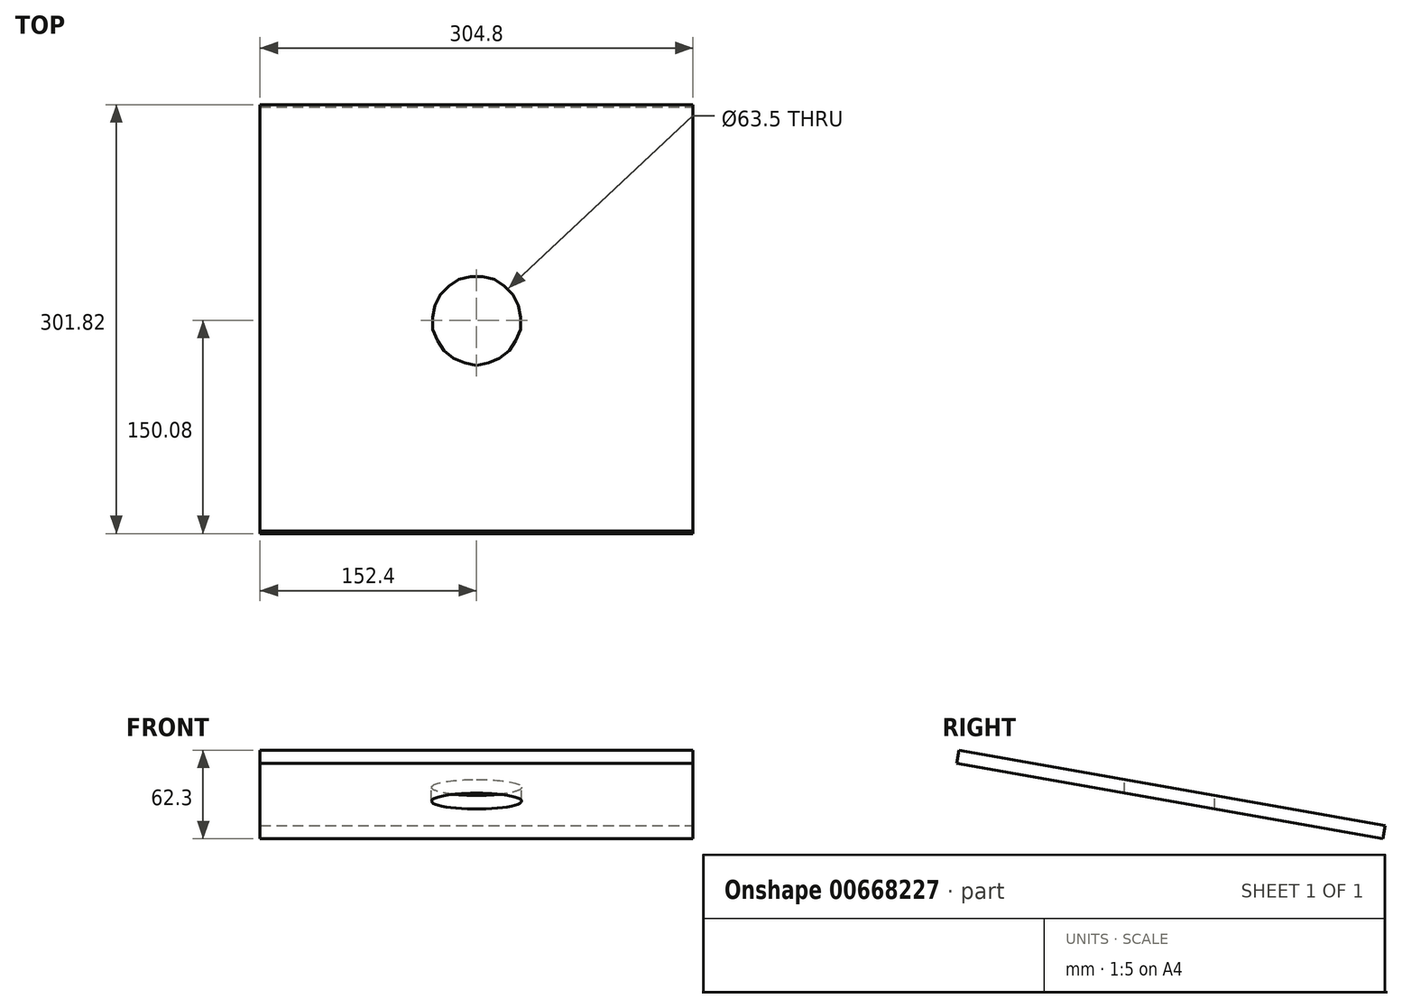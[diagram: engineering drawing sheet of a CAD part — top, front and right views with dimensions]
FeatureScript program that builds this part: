
annotation { "Feature Type Name" : "Feature", "Feature Type Description" : "" }
export const myFeature = defineFeature(function(context is Context, id is Id, definition is map)
    precondition{}
    {
        {
            var Q0;
            Q0=qCreatedBy(makeId("Top.planeOp"),FACE);
            var sketch = newSketch(context, id + "F0", { "sketchPlane" : qUnion([Q0])});
            skLineSegment(sketch, "E0", {"start": v(0, 0) * mm, "end": v(53.06, 0) * mm, "construction": true});
            skSolve(sketch);
        }
        {
            var Q0;
            Q0=sQuery(id+"F0.wireOp",EDGE,"E0");
            cPlane(context, id + "F1", {"entities" : qUnion([Q0]), "cplaneType" : CPlaneType.LINE_ANGLE, "offset" : 25 * mm, "angle" : 80 * degree, "width" : 150 * mm, "height" : 150 * mm});
        }
        {
            var Q0;
            Q0=qCreatedBy(id+"F1.planeOp",FACE);
            var sketch = newSketch(context, id + "F2", { "sketchPlane" : qUnion([Q0])});
            skLineSegment(sketch, "E1.bottom", {"start": v(-152.4, -152.4) * mm, "end": v(152.4, -152.4) * mm});
            skLineSegment(sketch, "E1.top", {"start": v(-152.4, 152.4) * mm, "end": v(152.4, 152.4) * mm});
            skLineSegment(sketch, "E1.left", {"start": v(-152.4, -152.4) * mm, "end": v(-152.4, 152.4) * mm});
            skLineSegment(sketch, "E1.right", {"start": v(152.4, -152.4) * mm, "end": v(152.4, 152.4) * mm});
            skLineSegment(sketch, "E2", {"start": v(-152.4, 152.4) * mm, "end": v(0, 0) * mm, "construction": true});
            skLineSegment(sketch, "E3", {"start": v(0, 0) * mm, "end": v(152.4, -152.4) * mm, "construction": true});
            skSolve(sketch);
        }
        {
            var Q0;
            Q0=makeQuery(id+"F2.imprint","IMPRINT",FACE,{"disambiguationData":[TD([[makeQuery(id+"F2.imprint","IMPRINT",EDGE,{"derivedFrom":sQuery(id+"F2.wireOp",EDGE,"E1.bottom")}),1.0]])]});
            extrude(context, id + "F3", {"entities" : qUnion([Q0]), "depth" : 9.52 * mm, "offsetDistance" : 25.4 * mm});
        }
        {
            var Q0;
            Q0=qCreatedBy(makeId("Top.planeOp"),FACE);
            var sketch = newSketch(context, id + "F4", { "sketchPlane" : qUnion([Q0])});
            skCircle(sketch, "E4", {"center": v(0, 0) * mm, "radius": 31.75 * mm});
            skSolve(sketch);
        }
        {
            var Q0;
            Q0 = qSketchRegion(id + "F4", true);
            extrude(context, id + "F5", {"entities" : qUnion([Q0]), "operationType" : NewBodyOperationType.REMOVE, "oppositeDirection" : true, "depth" : 25.4 * mm, "offsetDistance" : 25.4 * mm, "hasSecondDirection" : true, "secondDirectionOppositeDirection" : false, "secondDirectionDepth" : 25.4 * mm});
        }
    });
